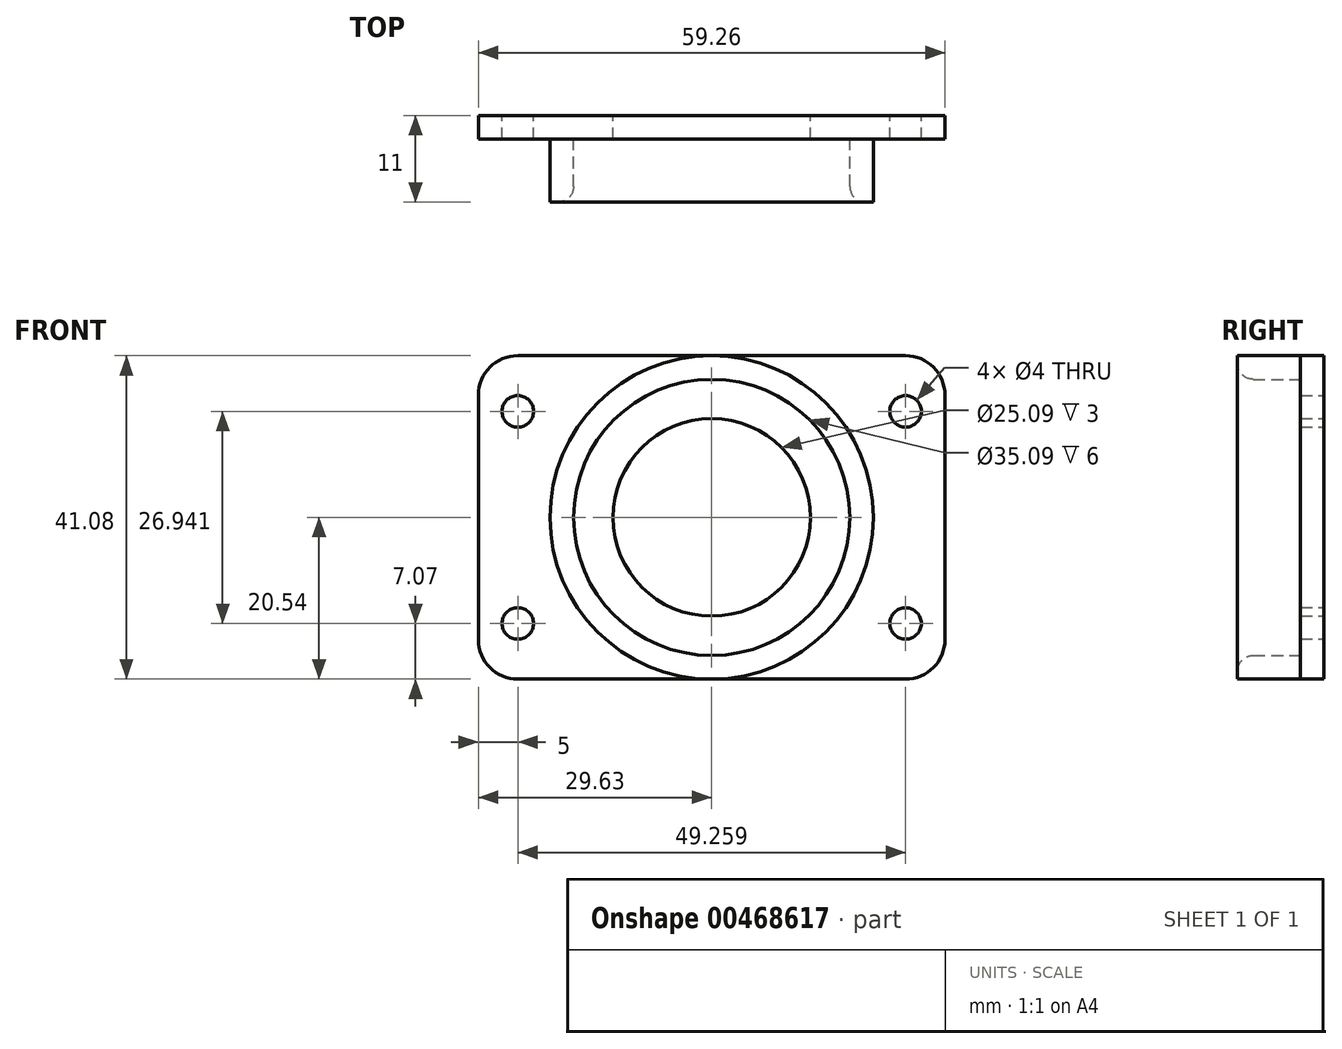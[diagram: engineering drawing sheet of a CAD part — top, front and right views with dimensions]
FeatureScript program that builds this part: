
annotation { "Feature Type Name" : "Feature", "Feature Type Description" : "" }
export const myFeature = defineFeature(function(context is Context, id is Id, definition is map)
    precondition{}
    {
        {
            var Q0;
            Q0=qCreatedBy(makeId("Front.planeOp"),FACE);
            var sketch = newSketch(context, id + "F0", { "sketchPlane" : qUnion([Q0])});
            skCircle(sketch, "E0", {"center": v(0, 0) * mm, "radius": 17.54 * mm});
            skLineSegment(sketch, "E1.bottom", {"start": v(-19.05, 20.54) * mm, "end": v(19.05, 20.54) * mm});
            skLineSegment(sketch, "E1.top", {"start": v(-19.05, -20.54) * mm, "end": v(19.05, -20.54) * mm});
            skLineSegment(sketch, "E1.left", {"start": v(-19.05, 20.54) * mm, "end": v(-19.05, -20.54) * mm});
            skLineSegment(sketch, "E1.right", {"start": v(19.05, 20.54) * mm, "end": v(19.05, -20.54) * mm});
            skLineSegment(sketch, "E2", {"start": v(-19.05, 20.54) * mm, "end": v(-57.15, 20.54) * mm});
            skLineSegment(sketch, "E3", {"start": v(-57.15, 20.54) * mm, "end": v(-57.15, -20.54) * mm, "construction": true});
            skLineSegment(sketch, "E4", {"start": v(-57.15, -20.54) * mm, "end": v(-19.05, -20.54) * mm});
            skLineSegment(sketch, "E5", {"start": v(19.05, -20.54) * mm, "end": v(57.15, -20.54) * mm});
            skLineSegment(sketch, "E6", {"start": v(57.15, -20.54) * mm, "end": v(57.15, 20.54) * mm, "construction": true});
            skLineSegment(sketch, "E7", {"start": v(57.15, 20.54) * mm, "end": v(19.05, 20.54) * mm});
            skCircle(sketch, "E8", {"center": v(-38.1, 0) * mm, "radius": 19.05 * mm, "construction": true});
            skPoint(sketch, "E8.centerSnap0", {"position": v(-38.1, 20.54) * mm});
            skPoint(sketch, "E8.centerSnap1", {"position": v(-19.05, 0) * mm});
            skCircle(sketch, "E9", {"center": v(38.1, 0) * mm, "radius": 19.05 * mm, "construction": true});
            skPoint(sketch, "E9.centerSnap0", {"position": v(38.1, 20.54) * mm});
            skLineSegment(sketch, "E10", {"start": v(-38.1, 0) * mm, "end": v(-19.05, 0) * mm, "construction": true});
            skLineSegment(sketch, "E11", {"start": v(-38.1, 0) * mm, "end": v(-24.63, 13.47) * mm, "construction": true});
            skLineSegment(sketch, "E12", {"start": v(-38.1, 0) * mm, "end": v(-24.63, -13.47) * mm, "construction": true});
            skLineSegment(sketch, "E13", {"start": v(38.1, 0) * mm, "end": v(19.05, 0) * mm, "construction": true});
            skLineSegment(sketch, "E14", {"start": v(24.63, 13.47) * mm, "end": v(38.1, 0) * mm, "construction": true});
            skLineSegment(sketch, "E15", {"start": v(24.63, -13.47) * mm, "end": v(38.1, 0) * mm, "construction": true});
            skCircle(sketch, "E16", {"center": v(-24.63, 13.47) * mm, "radius": 2 * mm});
            skCircle(sketch, "E17", {"center": v(-24.63, -13.47) * mm, "radius": 2 * mm});
            skCircle(sketch, "E18", {"center": v(24.63, -13.47) * mm, "radius": 2 * mm});
            skCircle(sketch, "E19", {"center": v(24.63, 13.47) * mm, "radius": 2 * mm});
            skLineSegment(sketch, "E20", {"start": v(-29.63, -20.54) * mm, "end": v(-29.63, 20.54) * mm});
            skLineSegment(sketch, "E21", {"start": v(29.63, -20.54) * mm, "end": v(29.63, 20.54) * mm});
            skLineSegment(sketch, "E22", {"start": v(-19.05, 0) * mm, "end": v(-29.63, 0) * mm, "construction": true});
            skLineSegment(sketch, "E23", {"start": v(19.05, 0) * mm, "end": v(29.63, 0) * mm, "construction": true});
            skCircle(sketch, "E24", {"center": v(0, 0) * mm, "radius": 12.54 * mm});
            skCircle(sketch, "E25", {"center": v(0, 0) * mm, "radius": 20.54 * mm});
            skSolve(sketch);
        }
        {
            var Q0;
            Q0=makeQuery(id+"F0.imprint","IMPRINT",FACE,{"disambiguationData":[TD([[makeQuery(id+"F0.imprint","IMPRINT",EDGE,{"derivedFrom":sQuery(id+"F0.wireOp",EDGE,"E0")}),-1.0]])]});
            var Q1;
            {var subQ1=sQuery(id+"F0.wireOp",EDGE,"E1.right");Q1=makeQuery(id+"F0.imprint","IMPRINT",FACE,{"disambiguationData":[TD([[makeQuery(id+"F0.imprint","IMPRINT",EDGE,{"derivedFrom":subQ1}),1.0]])]});}
            var Q2;
            {var subQ1=sQuery(id+"F0.wireOp",EDGE,"E1.left");Q2=makeQuery(id+"F0.imprint","IMPRINT",FACE,{"disambiguationData":[TD([[makeQuery(id+"F0.imprint","IMPRINT",EDGE,{"derivedFrom":subQ1}),-1.0]])]});}
            var Q3;
            {var subQ1=sQuery(id+"F0.wireOp",EDGE,"E1.bottom");var subQ3=sQuery(id+"F0.wireOp",EDGE,"E25");var subQ4=makeQuery(id+"F0.imprint","INTERSECT",VERTEX,{"derivedFrom":[subQ1,subQ3]});Q3=makeQuery(id+"F0.imprint","IMPRINT",FACE,{"disambiguationData":[TD([[makeQuery(id+"F0.imprint","IMPRINT",EDGE,{"disambiguationData":[TD([[subQ4,-1.0]])],"derivedFrom":subQ3}),-1.0]])]});}
            var Q4;
            {var subQ0=sQuery(id+"F0.wireOp",EDGE,"E25");var subQ1=sQuery(id+"F0.wireOp",EDGE,"E1.left");var subQ2=makeQuery(id+"F0.imprint","INTERSECT",VERTEX,{"disambiguationData":[OD(0.0)],"derivedFrom":[subQ1,subQ0]});Q4=makeQuery(id+"F0.imprint","IMPRINT",FACE,{"disambiguationData":[TD([[makeQuery(id+"F0.imprint","IMPRINT",EDGE,{"disambiguationData":[TD([[subQ2,-1.0]])],"derivedFrom":subQ1}),-1.0]])]});}
            var Q5;
            {var subQ0=sQuery(id+"F0.wireOp",EDGE,"E25");var subQ1=sQuery(id+"F0.wireOp",EDGE,"E1.right");var subQ2=makeQuery(id+"F0.imprint","INTERSECT",VERTEX,{"disambiguationData":[OD(0.0)],"derivedFrom":[subQ1,subQ0]});Q5=makeQuery(id+"F0.imprint","IMPRINT",FACE,{"disambiguationData":[TD([[makeQuery(id+"F0.imprint","IMPRINT",EDGE,{"disambiguationData":[TD([[subQ2,-1.0]])],"derivedFrom":subQ1}),1.0]])]});}
            var Q6;
            {var subQ1=sQuery(id+"F0.wireOp",EDGE,"E1.bottom");var subQ3=sQuery(id+"F0.wireOp",EDGE,"E25");var subQ4=makeQuery(id+"F0.imprint","INTERSECT",VERTEX,{"derivedFrom":[subQ1,subQ3]});Q6=makeQuery(id+"F0.imprint","IMPRINT",FACE,{"disambiguationData":[TD([[makeQuery(id+"F0.imprint","IMPRINT",EDGE,{"disambiguationData":[TD([[subQ4,1.0]])],"derivedFrom":subQ3}),-1.0]])]});}
            var Q7;
            {var subQ1=sQuery(id+"F0.wireOp",EDGE,"E1.top");var subQ3=sQuery(id+"F0.wireOp",EDGE,"E25");var subQ4=makeQuery(id+"F0.imprint","INTERSECT",VERTEX,{"derivedFrom":[subQ1,subQ3]});Q7=makeQuery(id+"F0.imprint","IMPRINT",FACE,{"disambiguationData":[TD([[makeQuery(id+"F0.imprint","IMPRINT",EDGE,{"disambiguationData":[TD([[subQ4,-1.0]])],"derivedFrom":subQ3}),-1.0]])]});}
            var Q8;
            {var subQ1=sQuery(id+"F0.wireOp",EDGE,"E1.top");var subQ3=sQuery(id+"F0.wireOp",EDGE,"E25");var subQ4=makeQuery(id+"F0.imprint","INTERSECT",VERTEX,{"derivedFrom":[subQ1,subQ3]});Q8=makeQuery(id+"F0.imprint","IMPRINT",FACE,{"disambiguationData":[TD([[makeQuery(id+"F0.imprint","IMPRINT",EDGE,{"disambiguationData":[TD([[subQ4,1.0]])],"derivedFrom":subQ3}),-1.0]])]});}
            extrude(context, id + "F1", {"entities" : qUnion([Q0, Q1, Q2, Q3, Q4, Q5, Q6, Q7, Q8]), "depth" : 3 * mm, "offsetDistance" : 25 * mm});
        }
        {
            var Q0;
            Q0=makeQuery(id+"F0.imprint","IMPRINT",FACE,{"disambiguationData":[TD([[makeQuery(id+"F0.imprint","IMPRINT",EDGE,{"derivedFrom":sQuery(id+"F0.wireOp",EDGE,"E0")}),1.0]])]});
            extrude(context, id + "F2", {"entities" : qUnion([Q0]), "operationType" : NewBodyOperationType.ADD, "depth" : 3 * mm, "offsetDistance" : 25 * mm});
        }
        {
            var Q0;
            Q0=makeQuery(id+"F0.imprint","IMPRINT",FACE,{"disambiguationData":[TD([[makeQuery(id+"F0.imprint","IMPRINT",EDGE,{"derivedFrom":sQuery(id+"F0.wireOp",EDGE,"E0")}),-1.0]])]});
            var Q1;
            {var subQ0=sQuery(id+"F0.wireOp",EDGE,"E25");var subQ1=sQuery(id+"F0.wireOp",EDGE,"E1.left");var subQ2=makeQuery(id+"F0.imprint","INTERSECT",VERTEX,{"disambiguationData":[OD(0.0)],"derivedFrom":[subQ1,subQ0]});Q1=makeQuery(id+"F0.imprint","IMPRINT",FACE,{"disambiguationData":[TD([[makeQuery(id+"F0.imprint","IMPRINT",EDGE,{"disambiguationData":[TD([[subQ2,-1.0]])],"derivedFrom":subQ1}),-1.0]])]});}
            var Q2;
            {var subQ0=sQuery(id+"F0.wireOp",EDGE,"E25");var subQ1=sQuery(id+"F0.wireOp",EDGE,"E1.right");var subQ2=makeQuery(id+"F0.imprint","INTERSECT",VERTEX,{"disambiguationData":[OD(0.0)],"derivedFrom":[subQ1,subQ0]});Q2=makeQuery(id+"F0.imprint","IMPRINT",FACE,{"disambiguationData":[TD([[makeQuery(id+"F0.imprint","IMPRINT",EDGE,{"disambiguationData":[TD([[subQ2,-1.0]])],"derivedFrom":subQ1}),1.0]])]});}
            extrude(context, id + "F3", {"entities" : qUnion([Q0, Q1, Q2]), "operationType" : NewBodyOperationType.ADD, "depth" : 11 * mm, "offsetDistance" : 25 * mm});
        }
        {
            var Q0;
            Q0=makeQuery(id+"F1.opExtrude","SWEPT_EDGE",EDGE,{"disambiguationData":[OSD([sQuery(id+"F0.wireOp",EDGE,"E2"),sQuery(id+"F0.wireOp",EDGE,"E20")])]});
            var Q1;
            Q1=makeQuery(id+"F1.opExtrude","SWEPT_EDGE",EDGE,{"disambiguationData":[OSD([sQuery(id+"F0.wireOp",EDGE,"E4"),sQuery(id+"F0.wireOp",EDGE,"E20")])]});
            var Q2;
            Q2=makeQuery(id+"F1.opExtrude","SWEPT_EDGE",EDGE,{"disambiguationData":[OSD([sQuery(id+"F0.wireOp",EDGE,"E5"),sQuery(id+"F0.wireOp",EDGE,"E21")])]});
            var Q3;
            Q3=makeQuery(id+"F1.opExtrude","SWEPT_EDGE",EDGE,{"disambiguationData":[OSD([sQuery(id+"F0.wireOp",EDGE,"E7"),sQuery(id+"F0.wireOp",EDGE,"E21")])]});
            fillet(context, id + "F4", {"entities" : qUnion([Q0, Q1, Q2, Q3]), "radius" : 5 * mm, "tangentPropagation" : true, "allowEdgeOverflow" : false});
        }
        {
            var Q0;
            Q0=makeQuery(id+"F3.opExtrude","CAP_EDGE",EDGE,{"disambiguationData":[OSD([sQuery(id+"F0.wireOp",EDGE,"E0")])],"isStart":false});
            fillet(context, id + "F5", {"entities" : qUnion([Q0]), "radius" : 2 * mm, "tangentPropagation" : true, "allowEdgeOverflow" : false});
        }
    });
